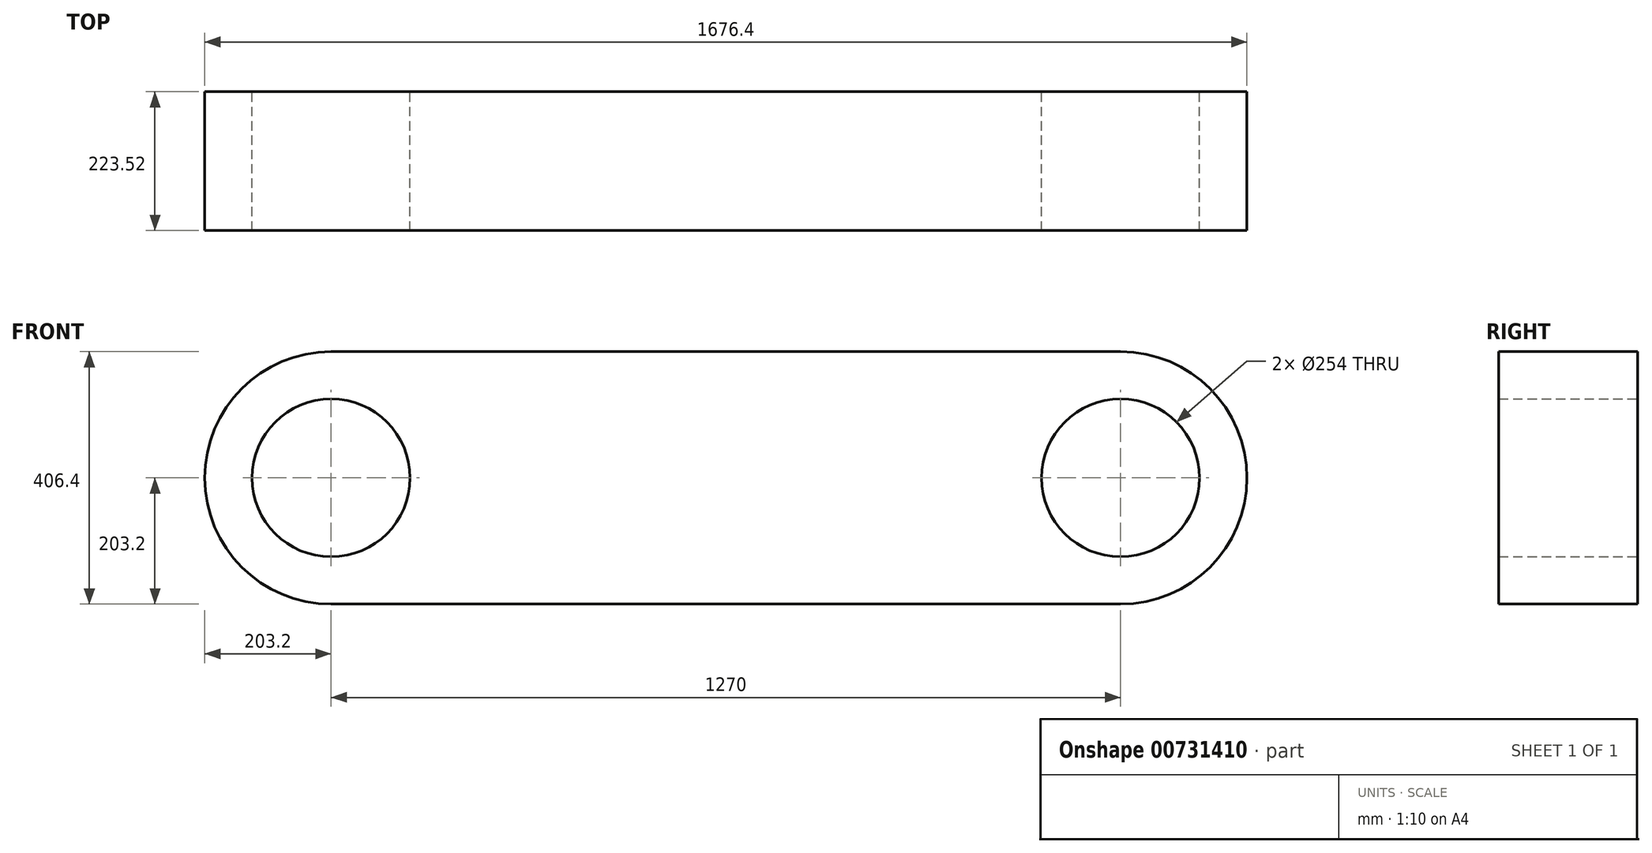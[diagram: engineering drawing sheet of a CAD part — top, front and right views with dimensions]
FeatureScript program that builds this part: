
annotation { "Feature Type Name" : "Feature", "Feature Type Description" : "" }
export const myFeature = defineFeature(function(context is Context, id is Id, definition is map)
    precondition{}
    {
        {
            var Q0;
            Q0=qCreatedBy(makeId("Front.planeOp"),FACE);
            var sketch = newSketch(context, id + "F0", { "sketchPlane" : qUnion([Q0])});
            skLineSegment(sketch, "E0.bottom", {"start": v(-635, 203.2) * mm, "end": v(635, 203.2) * mm});
            skLineSegment(sketch, "E0.top", {"start": v(-635, -203.2) * mm, "end": v(635, -203.2) * mm});
            skLineSegment(sketch, "E1.left", {"start": v(-635, 203.2) * mm, "end": v(-635, 203.2) * mm});
            skLineSegment(sketch, "E1.right", {"start": v(635, 203.2) * mm, "end": v(635, 203.2) * mm});
            skArc(sketch, "E2", {"start": v(635, -203.2) * mm, "mid": v(838.2, 0) * mm, "end": v(635, 203.2) * mm});
            skArc(sketch, "E3", {"start": v(-635, 203.2) * mm, "mid": v(-838.2, 0) * mm, "end": v(-635, -203.2) * mm});
            skSolve(sketch);
        }
        {
            var Q0;
            Q0 = qSketchRegion(id + "F0", true);
            extrude(context, id + "F1", {"entities" : qUnion([Q0]), "oppositeDirection" : true, "depth" : 223.52 * mm, "offsetDistance" : 25.4 * mm});
        }
        {
            var Q0;
            Q0=makeQuery(id+"F1.opExtrude","CAP_FACE",FACE,{"disambiguationData":[OSD([sQuery(id+"F0.wireOp",EDGE,"E0.top"),sQuery(id+"F0.wireOp",EDGE,"E0.bottom"),sQuery(id+"F0.wireOp",EDGE,"E2"),sQuery(id+"F0.wireOp",EDGE,"E3")])],"isStart":false});
            var sketch = newSketch(context, id + "F2", { "sketchPlane" : qUnion([Q0])});
            skCircle(sketch, "E4", {"center": v(-635, 0) * mm, "radius": 127 * mm});
            skCircle(sketch, "E5", {"center": v(635, 0) * mm, "radius": 127 * mm});
            skSolve(sketch);
        }
        {
            var Q0;
            Q0 = qSketchRegion(id + "F2", true);
            extrude(context, id + "F3", {"entities" : qUnion([Q0]), "operationType" : NewBodyOperationType.REMOVE, "oppositeDirection" : true, "depth" : 833.12 * mm, "offsetDistance" : 25.4 * mm});
        }
    });
